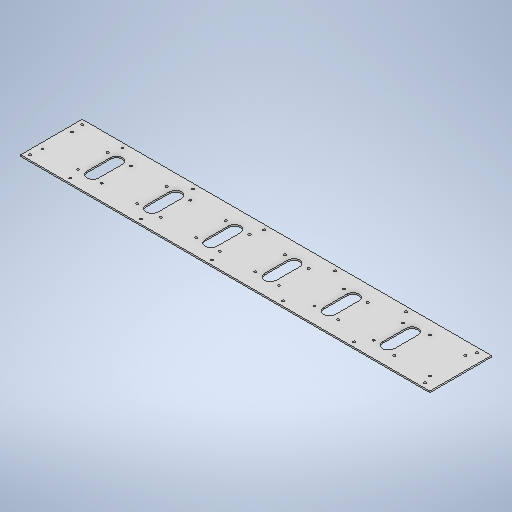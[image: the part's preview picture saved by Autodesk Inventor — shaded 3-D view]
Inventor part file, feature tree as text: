
AUTODESK INVENTOR PART (.ipt)
format: ipt  version: 2025.1 (Build 291241000, 241)  size: 400,896 bytes
history: native  units: in
note: dims shown in document units (in); Inventor stores cm internally (conversion verified against a paired STEP export)
features: extrude x1, sketch x1
ambient origin geometry x8: Origin, YZ Plane, XZ Plane, XY Plane, X Axis, Y Axis, Z Axis, Center Point
bodies: Solid1 (feature_tree)
feature tree (2):
  extrude  "Extrusion1"  Depth=0.125in
  sketch  "Sketch1"  dims[d8=34.6in d9=2.6in d10=0.8in d11=90.0deg d12=34.6in d14=0.8in d15=0.0in d16=0.2in d17=6.0in d19=0.2in d20=6.0in d21=0.2in d22=6.0in d23=0.2in d24=6.0in d25=0.2in d26=6.0in d27=0.2in d28=0.4in d29=90.0deg d30=0.4in d31=90.0deg d32=0.2in d33=1.1in d34=90.0deg d35=1.1in d36=90.0deg d37=0.2in d38=3.0in d39=0.0in d40=0.2in d41=1.0in d43=1.0in d46=0.5in d47=90.0deg d48=0.5in d51=0.5in d52=0.0in d53=1.25in d54=90.0deg d55=0.2in d56=3.0in d57=0.0in d58=0.2in d59=2.0in d60=180.0deg d61=1.0in d62=0.2in d63=3.0in d64=0.2in d65=2.0in d66=1.0in d67=0.2in d68=3.0in d69=0.2in d70=2.0in d71=1.0in d72=0.2in d73=3.0in d74=0.2in d75=2.0in d76=1.0in d77=0.2in d78=3.0in d79=0.2in d80=2.0in d81=1.0in d82=0.2in d83=3.0in d84=0.2in d85=2.0in d86=0.125in d87=0.0in]
